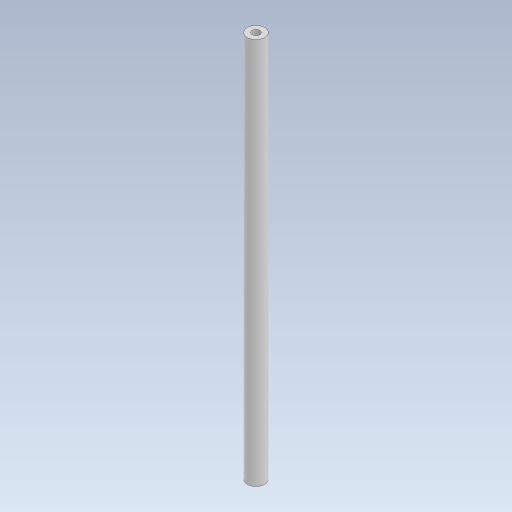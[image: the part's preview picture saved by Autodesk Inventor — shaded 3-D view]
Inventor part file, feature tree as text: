
AUTODESK INVENTOR PART (.ipt)
format: ipt  version: 2023.5 (Build 275446000, 446)  size: 210,432 bytes
history: native  units: mm
features: extrude x2, sketch x2
ambient origin geometry x8: Origin, YZ Plane, XZ Plane, XY Plane, X Axis, Y Axis, Z Axis, Center Point
bodies: Solid1 (feature_tree)
feature tree (4):
  extrude  "Extrusion1"  Depth=150.0mm TaperAngle=0.0deg
  extrude  "Extrusion2"  Depth=10.0mm TaperAngle=0.0deg
  sketch  "Sketch1"  dims[d0=6.8mm d1=150.0mm d2=0.0mm]
  sketch  "Sketch2"  dims[d3=3.0mm d4=10.0mm d5=0.0mm]
